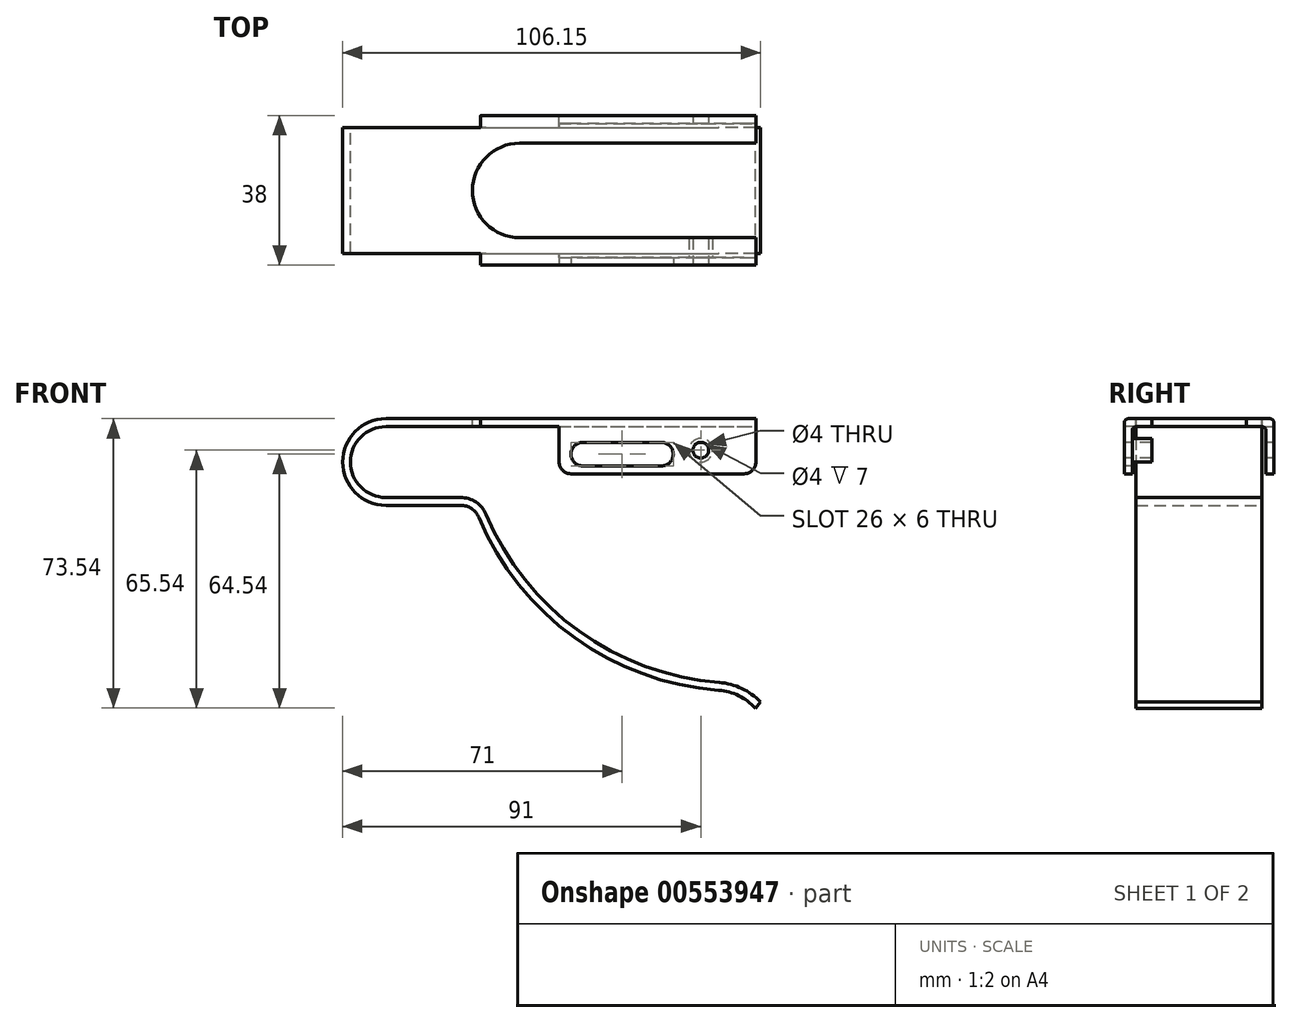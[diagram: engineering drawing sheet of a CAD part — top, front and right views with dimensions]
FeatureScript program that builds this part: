
annotation { "Feature Type Name" : "Feature", "Feature Type Description" : "" }
export const myFeature = defineFeature(function(context is Context, id is Id, definition is map)
    precondition{}
    {
        {
            var Q0;
            Q0=qCreatedBy(makeId("Front.planeOp"),FACE);
            var sketch = newSketch(context, id + "F0", { "sketchPlane" : qUnion([Q0])});
            skArc(sketch, "E0", {"start": v(0, 11) * mm, "mid": v(-11, 0) * mm, "end": v(0, -11) * mm});
            skLineSegment(sketch, "E1", {"start": v(0, 11) * mm, "end": v(94, 11) * mm});
            skLineSegment(sketch, "E2", {"start": v(0, -11) * mm, "end": v(19, -11) * mm});
            skArc(sketch, "E3", {"start": v(23.61, -14.06) * mm, "mid": v(47.9, -44.6) * mm, "end": v(84.55, -58) * mm});
            skArc(sketch, "E4", {"start": v(93.86, -62.54) * mm, "mid": v(89.64, -59.38) * mm, "end": v(84.55, -58) * mm});
            skPoint(sketch, "E5.visualSharp", {"position": v(22.4, -11) * mm});
            skArc(sketch, "E5.filletArc", {"start": v(23.61, -14.06) * mm, "mid": v(21.77, -11.84) * mm, "end": v(19, -11) * mm});
            skLineSegment(sketch, "E6.0", {"start": v(0, 9) * mm, "end": v(94, 9) * mm});
            skArc(sketch, "E6.1", {"start": v(0, 9) * mm, "mid": v(-9, 0) * mm, "end": v(0, -9) * mm});
            skArc(sketch, "E6.2", {"start": v(95.15, -61) * mm, "mid": v(90.4, -57.52) * mm, "end": v(84.7, -56) * mm});
            skArc(sketch, "E6.3", {"start": v(25.45, -13.3) * mm, "mid": v(49.07, -42.99) * mm, "end": v(84.7, -56) * mm});
            skArc(sketch, "E6.4", {"start": v(25.45, -13.3) * mm, "mid": v(22.88, -10.17) * mm, "end": v(19, -9) * mm});
            skLineSegment(sketch, "E6.5", {"start": v(0, -9) * mm, "end": v(19, -9) * mm});
            skLineSegment(sketch, "E7", {"start": v(94, 11) * mm, "end": v(94, 9) * mm});
            skLineSegment(sketch, "E8", {"start": v(95.15, -61) * mm, "end": v(93.86, -62.54) * mm});
            skLineSegment(sketch, "E9", {"start": v(107.63, -61.05) * mm, "end": v(113.07, -61.05) * mm});
            skSolve(sketch);
        }
        {
            var Q0;
            Q0=qSketchRegion(id+"F0",true);
            extrude(context, id + "F1", {"entities" : qUnion([Q0]), "depth" : 16 * mm});
        }
        {
            var Q0;
            Q0=makeQuery(id+"F1.opExtrude","SWEPT_FACE",FACE,{"disambiguationData":[OSD([sQuery(id+"F0.wireOp",EDGE,"E1")])]});
            var sketch = newSketch(context, id + "F2", { "sketchPlane" : qUnion([Q0])});
            skLineSegment(sketch, "E10.bottom", {"start": v(94, -16) * mm, "end": v(24, -16) * mm});
            skLineSegment(sketch, "E10.top", {"start": v(94, -19) * mm, "end": v(24, -19) * mm});
            skLineSegment(sketch, "E10.left", {"start": v(94, -16) * mm, "end": v(94, -19) * mm});
            skLineSegment(sketch, "E10.right", {"start": v(24, -16) * mm, "end": v(24, -19) * mm});
            skSolve(sketch);
        }
        {
            var Q0;
            Q0=qSketchRegion(id+"F2",true);
            extrude(context, id + "F3", {"entities" : qUnion([Q0]), "operationType" : NewBodyOperationType.ADD, "oppositeDirection" : true, "depth" : 2 * mm});
        }
        {
            var Q0;
            Q0=makeQuery(id+"F3.opExtrude","SWEPT_FACE",FACE,{"disambiguationData":[OSD([sQuery(id+"F2.wireOp",EDGE,"E10.top")])]});
            var sketch = newSketch(context, id + "F4", { "sketchPlane" : qUnion([Q0])});
            skLineSegment(sketch, "E11.bottom", {"start": v(94, 11) * mm, "end": v(44, 11) * mm});
            skLineSegment(sketch, "E11.top", {"start": v(94, -3) * mm, "end": v(44, -3) * mm});
            skLineSegment(sketch, "E11.left", {"start": v(94, 11) * mm, "end": v(94, -3) * mm});
            skLineSegment(sketch, "E11.right", {"start": v(44, 11) * mm, "end": v(44, -3) * mm});
            skSolve(sketch);
        }
        {
            var Q0;
            Q0=qSketchRegion(id+"F4",true);
            extrude(context, id + "F5", {"entities" : qUnion([Q0]), "operationType" : NewBodyOperationType.ADD, "oppositeDirection" : true, "depth" : 2 * mm});
        }
        {
            var Q0;
            Q0=makeQuery(id+"F3.opExtrude","CAP_EDGE",EDGE,{"disambiguationData":[OSD([sQuery(id+"F2.wireOp",EDGE,"E10.top")])],"isStart":true});
            var Q1;
            Q1=makeQuery(id+"F5.boolean.opBoolean","INTERSECT",EDGE,{"derivedFrom":[makeQuery(id+"F3.boolean.opBoolean","MERGE",FACE,{"derivedFrom":[makeQuery(id+"F1.opExtrude","SWEPT_FACE",FACE,{"disambiguationData":[OSD([sQuery(id+"F0.wireOp",EDGE,"E6.0")])]}),makeQuery(id+"F3.opExtrude","CAP_FACE",FACE,{"disambiguationData":[OSD([sQuery(id+"F2.wireOp",EDGE,"E10.bottom"),sQuery(id+"F2.wireOp",EDGE,"E10.top"),sQuery(id+"F2.wireOp",EDGE,"E10.left"),sQuery(id+"F2.wireOp",EDGE,"E10.right")])],"isStart":false})]}),makeQuery(id+"F5.opExtrude","CAP_FACE",FACE,{"disambiguationData":[OSD([sQuery(id+"F4.wireOp",EDGE,"E11.bottom"),sQuery(id+"F4.wireOp",EDGE,"E11.top"),sQuery(id+"F4.wireOp",EDGE,"E11.left"),sQuery(id+"F4.wireOp",EDGE,"E11.right")])],"isStart":false})]});
            fillet(context, id + "F6", {"entities" : qUnion([Q0, Q1]), "radius" : 1 * mm, "tangentPropagation" : true, "allowEdgeOverflow" : false});
        }
        {
            var Q0;
            Q0=makeQuery(id+"F1.opExtrude","SWEPT_BODY",BODY,{"disambiguationData":[OSD([sQuery(id+"F0.wireOp",EDGE,"E0"),sQuery(id+"F0.wireOp",EDGE,"E1"),sQuery(id+"F0.wireOp",EDGE,"E2"),sQuery(id+"F0.wireOp",EDGE,"E3"),sQuery(id+"F0.wireOp",EDGE,"E4"),sQuery(id+"F0.wireOp",EDGE,"E5.filletArc"),sQuery(id+"F0.wireOp",EDGE,"E6.0"),sQuery(id+"F0.wireOp",EDGE,"E6.1"),sQuery(id+"F0.wireOp",EDGE,"E6.2"),sQuery(id+"F0.wireOp",EDGE,"E6.3"),sQuery(id+"F0.wireOp",EDGE,"E6.4"),sQuery(id+"F0.wireOp",EDGE,"E6.5"),sQuery(id+"F0.wireOp",EDGE,"E7"),sQuery(id+"F0.wireOp",EDGE,"E8")])]});
            var Q1;
            Q1=qCreatedBy(makeId("Front.planeOp"),FACE);
            mirror(context, id + "F7", {"operationType" : NewBodyOperationType.ADD, "entities" : qUnion([Q0]), "mirrorPlane" : qUnion([Q1])});
        }
        {
            var Q0;
            {var subQ0=makeQuery(id+"F3.boolean.opBoolean","MERGE",FACE,{"derivedFrom":[makeQuery(id+"F1.opExtrude","SWEPT_FACE",FACE,{"disambiguationData":[OSD([sQuery(id+"F0.wireOp",EDGE,"E1")])]}),makeQuery(id+"F3.opExtrude","CAP_FACE",FACE,{"disambiguationData":[OSD([sQuery(id+"F2.wireOp",EDGE,"E10.bottom"),sQuery(id+"F2.wireOp",EDGE,"E10.top"),sQuery(id+"F2.wireOp",EDGE,"E10.left"),sQuery(id+"F2.wireOp",EDGE,"E10.right")])],"isStart":true})]});Q0=makeQuery(id+"F7.boolean.opBoolean","MERGE",FACE,{"derivedFrom":[subQ0,makeQuery(id+"F7.opPattern","COPY",FACE,{"derivedFrom":subQ0,"instanceName":"1"})]});}
            var sketch = newSketch(context, id + "F8", { "sketchPlane" : qUnion([Q0])});
            skArc(sketch, "E12", {"start": v(34, 12) * mm, "mid": v(22, 0) * mm, "end": v(34, -12) * mm});
            skLineSegment(sketch, "E13", {"start": v(34, -12) * mm, "end": v(94, -12) * mm});
            skLineSegment(sketch, "E14", {"start": v(34, 12) * mm, "end": v(94, 12) * mm});
            skSolve(sketch);
        }
        {
            var Q0;
            Q0=makeQuery(id+"F8.imprint","IMPRINT",FACE,{"disambiguationData":[TD([[makeQuery(id+"F8.imprint","IMPRINT",EDGE,{"derivedFrom":sQuery(id+"F8.wireOp",EDGE,"E12")}),1.0]])]});
            extrude(context, id + "F9", {"entities" : qUnion([Q0]), "operationType" : NewBodyOperationType.REMOVE, "oppositeDirection" : true, "depth" : 2 * mm});
        }
        {
            var Q0;
            Q0=makeQuery(id+"F5.boolean.opBoolean","MERGE",FACE,{"derivedFrom":[makeQuery(id+"F3.opExtrude","SWEPT_FACE",FACE,{"disambiguationData":[OSD([sQuery(id+"F2.wireOp",EDGE,"E10.top")])]}),makeQuery(id+"F5.opExtrude","CAP_FACE",FACE,{"disambiguationData":[OSD([sQuery(id+"F4.wireOp",EDGE,"E11.bottom"),sQuery(id+"F4.wireOp",EDGE,"E11.top"),sQuery(id+"F4.wireOp",EDGE,"E11.left"),sQuery(id+"F4.wireOp",EDGE,"E11.right")])],"isStart":true})]});
            var sketch = newSketch(context, id + "F10", { "sketchPlane" : qUnion([Q0])});
            skLineSegment(sketch, "E15", {"start": v(50, 2) * mm, "end": v(70, 2) * mm});
            skArc(sketch, "E16.0.startCap", {"start": v(50, -1) * mm, "mid": v(47, 2) * mm, "end": v(50, 5) * mm});
            skArc(sketch, "E16.0.endCap", {"start": v(70, 5) * mm, "mid": v(73, 2) * mm, "end": v(70, -1) * mm});
            skLineSegment(sketch, "E16.0.left", {"start": v(50, 5) * mm, "end": v(70, 5) * mm});
            skLineSegment(sketch, "E16.0.right", {"start": v(50, -1) * mm, "end": v(70, -1) * mm});
            skSolve(sketch);
        }
        {
            var Q0;
            Q0=qSketchRegion(id+"F10",true);
            extrude(context, id + "F11", {"entities" : qUnion([Q0]), "operationType" : NewBodyOperationType.REMOVE, "oppositeDirection" : true, "depth" : 25 * mm});
        }
        {
            var Q0;
            Q0=makeQuery(id+"F5.boolean.opBoolean","MERGE",FACE,{"derivedFrom":[makeQuery(id+"F3.opExtrude","SWEPT_FACE",FACE,{"disambiguationData":[OSD([sQuery(id+"F2.wireOp",EDGE,"E10.top")])]}),makeQuery(id+"F5.opExtrude","CAP_FACE",FACE,{"disambiguationData":[OSD([sQuery(id+"F4.wireOp",EDGE,"E11.bottom"),sQuery(id+"F4.wireOp",EDGE,"E11.top"),sQuery(id+"F4.wireOp",EDGE,"E11.left"),sQuery(id+"F4.wireOp",EDGE,"E11.right")])],"isStart":true})]});
            var sketch = newSketch(context, id + "F12", { "sketchPlane" : qUnion([Q0])});
            skPoint(sketch, "E17", {"position": v(80, 3) * mm});
            skSolve(sketch);
        }
        {
            var Q0;
            Q0=sQuery(id+"F12.wireOp",VERTEX,"E17");
            var Q1;
            Q1=makeQuery(id+"F1.opExtrude","SWEPT_BODY",BODY,{"disambiguationData":[OSD([sQuery(id+"F0.wireOp",EDGE,"E0"),sQuery(id+"F0.wireOp",EDGE,"E1"),sQuery(id+"F0.wireOp",EDGE,"E2"),sQuery(id+"F0.wireOp",EDGE,"E3"),sQuery(id+"F0.wireOp",EDGE,"E4"),sQuery(id+"F0.wireOp",EDGE,"E5.filletArc"),sQuery(id+"F0.wireOp",EDGE,"E6.0"),sQuery(id+"F0.wireOp",EDGE,"E6.1"),sQuery(id+"F0.wireOp",EDGE,"E6.2"),sQuery(id+"F0.wireOp",EDGE,"E6.3"),sQuery(id+"F0.wireOp",EDGE,"E6.4"),sQuery(id+"F0.wireOp",EDGE,"E6.5"),sQuery(id+"F0.wireOp",EDGE,"E7"),sQuery(id+"F0.wireOp",EDGE,"E8")])]});
            hole(context, id + "F13", {"style" : HoleStyle.SIMPLE, "endStyle" : HoleEndStyle.BLIND, "holeDiameter" : 4 * mm, "holeDepth" : 50 * mm, "isTappedThrough" : true, "tappedDepth" : 12 * mm, "tapClearance" : 3, "locations" : qUnion([Q0]), "scope" : qUnion([Q1])});
        }
        {
            var Q0;
            Q0=makeQuery(id+"F5.opExtrude","CAP_FACE",FACE,{"disambiguationData":[OSD([sQuery(id+"F4.wireOp",EDGE,"E11.bottom"),sQuery(id+"F4.wireOp",EDGE,"E11.top"),sQuery(id+"F4.wireOp",EDGE,"E11.left"),sQuery(id+"F4.wireOp",EDGE,"E11.right")])],"isStart":false});
            var sketch = newSketch(context, id + "F14", { "sketchPlane" : qUnion([Q0])});
            skCircle(sketch, "E18.0", {"center": v(-80, 3) * mm, "radius": 2 * mm});
            skCircle(sketch, "E19.0", {"center": v(-80, 3) * mm, "radius": 3 * mm});
            skSolve(sketch);
        }
        {
            var Q0;
            Q0=qSketchRegion(id+"F14",true);
            extrude(context, id + "F15", {"entities" : qUnion([Q0]), "operationType" : NewBodyOperationType.ADD, "depth" : 5 * mm});
        }
        {
            var Q0;
            Q0=makeQuery(id+"F5.opExtrude","SWEPT_EDGE",EDGE,{"disambiguationData":[OSD([sQuery(id+"F4.wireOp",EDGE,"E11.top"),sQuery(id+"F4.wireOp",EDGE,"E11.left")])]});
            var Q1;
            Q1=makeQuery(id+"F7.opPattern","COPY",EDGE,{"derivedFrom":makeQuery(id+"F5.opExtrude","SWEPT_EDGE",EDGE,{"disambiguationData":[OSD([sQuery(id+"F4.wireOp",EDGE,"E11.top"),sQuery(id+"F4.wireOp",EDGE,"E11.left")])]}),"instanceName":"1"});
            var Q2;
            Q2=makeQuery(id+"F5.opExtrude","SWEPT_EDGE",EDGE,{"disambiguationData":[OSD([sQuery(id+"F4.wireOp",EDGE,"E11.top"),sQuery(id+"F4.wireOp",EDGE,"E11.right")])]});
            var Q3;
            Q3=makeQuery(id+"F7.opPattern","COPY",EDGE,{"derivedFrom":makeQuery(id+"F5.opExtrude","SWEPT_EDGE",EDGE,{"disambiguationData":[OSD([sQuery(id+"F4.wireOp",EDGE,"E11.top"),sQuery(id+"F4.wireOp",EDGE,"E11.right")])]}),"instanceName":"1"});
            fillet(context, id + "F16", {"entities" : qUnion([Q0, Q1, Q2, Q3]), "radius" : 3 * mm, "tangentPropagation" : true, "allowEdgeOverflow" : false});
        }
    });
